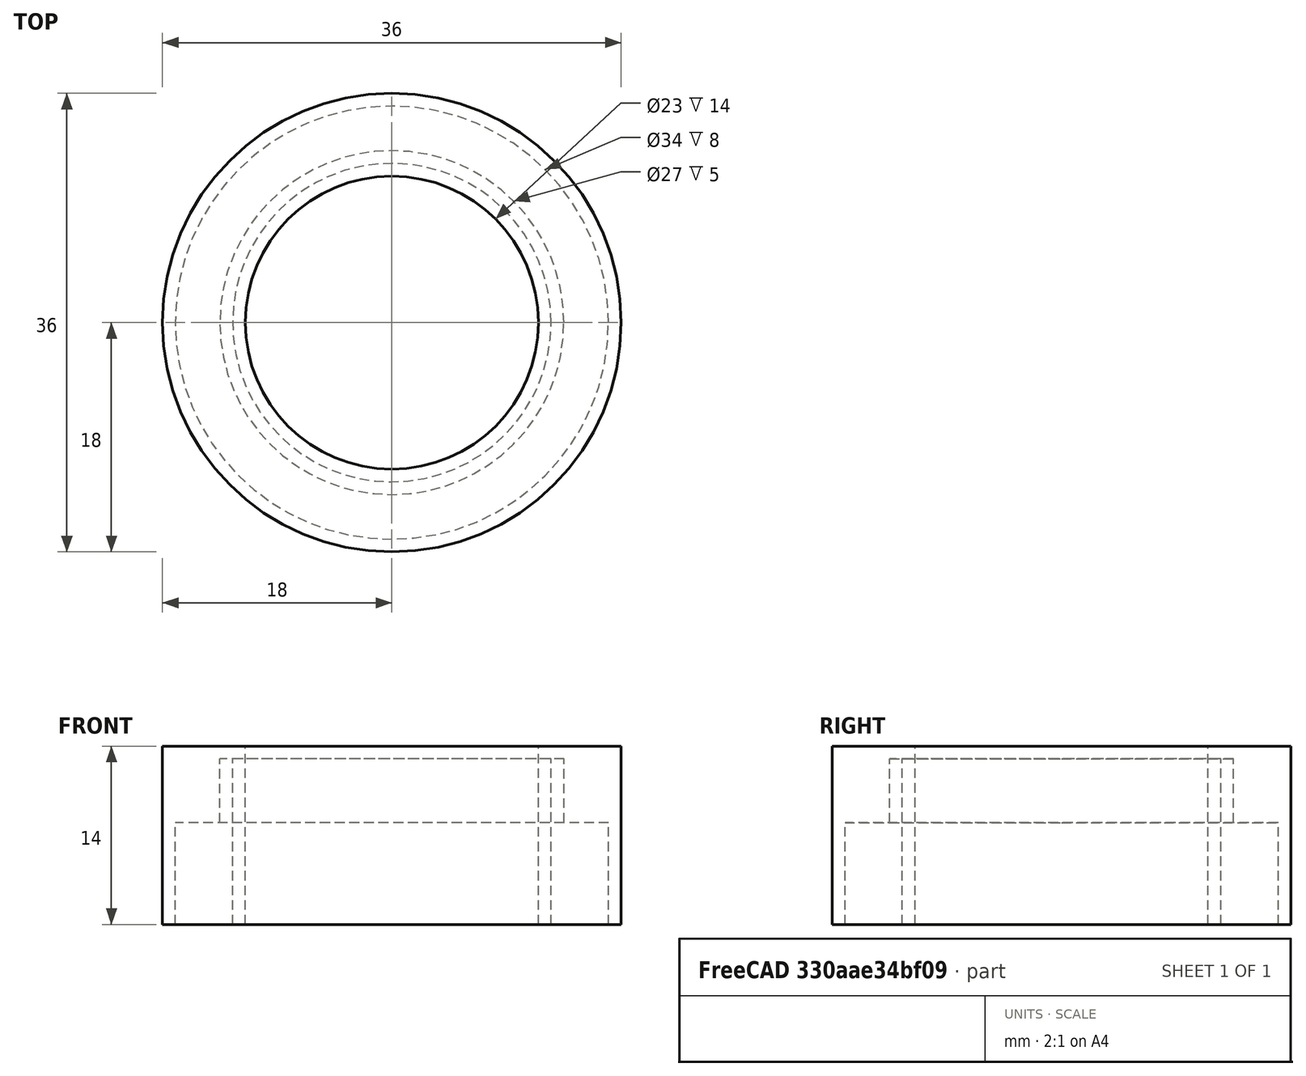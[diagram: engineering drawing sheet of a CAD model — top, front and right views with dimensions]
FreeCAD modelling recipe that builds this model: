
FCSTD DOCUMENT  (FreeCAD 0.17R13509 (Git))
Label: FTInsulator1_negative_tall
License: All rights reserved
LicenseURL: http://en.wikipedia.org/wiki/All_rights_reserved
objects: Part::Cylinder×5, Part::Cut×3, Part::MultiFuse×1
note: 9 computed .brp shape members not serialized (recipe doc carries the construction recipe); baked Part::Feature solids carry a one-line shape summary decoded from their .brp

FEATURE [Part::Cylinder] Cylinder  label="Lug"
  Angle = 360
  AttacherType = Attacher::AttachEngine3D
  Height = 8
  Radius = 17
  expr: Radius = 34 / 2
FEATURE [Part::Cylinder] Cylinder001  label="InnerHole"
  Angle = 360
  AttacherType = Attacher::AttachEngine3D
  Height = 24
  Placement = pos=(0,0,-5) rot=(0,0,1;0rad)
  Radius = 12.5
FEATURE [Part::Cylinder] Cylinder002  label="Sleeve"
  Angle = 360
  AttacherType = Attacher::AttachEngine3D
  Height = 13
  Radius = 13.5
FEATURE [Part::Cylinder] Cylinder003  label="MaterialSaving"
  Angle = 360
  AttacherType = Attacher::AttachEngine3D
  Height = 25
  Radius = 11.5
FEATURE [Part::Cylinder] Cylinder004  label="Negative"
  Angle = 360
  AttacherType = Attacher::AttachEngine3D
  Height = 14
  Radius = 18
FEATURE [Part::MultiFuse] Fusion
  Shapes = -> [Cylinder,Cylinder002]
FEATURE [Part::Cut] Cut
  Base = -> Fusion
  Tool = -> Cylinder001
FEATURE [Part::Cut] Cut001
  Base = -> Cylinder004
  Tool = -> Cylinder003
FEATURE [Part::Cut] Cut002
  Base = -> Cut001
  Tool = -> Cut
